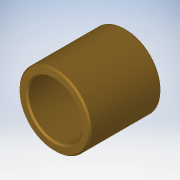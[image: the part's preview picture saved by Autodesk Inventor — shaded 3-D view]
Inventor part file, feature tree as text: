
AUTODESK INVENTOR PART (.ipt)
format: ipt  version: 2018.2 (Build 222227000, 227)  size: 112,640 bytes
history: native  units: mm
features: extrude x1, chamfer x1, sketch x1
ambient origin geometry x8: Origin, YZ Plane, XZ Plane, XY Plane, X Axis, Y Axis, Z Axis, Center Point
bodies: Solid1 (feature_tree)
feature tree (3):
  extrude  "Extrusion1"  Depth=12.7mm
  chamfer  "Chamfer1"  Distance=12.7mm
  sketch  "Sketch1"  dims[d0=12.7mm d1=9.525mm d2=12.7mm d3=0.0mm d4=0.25mm d5=2.0mm d6=45.0deg]
